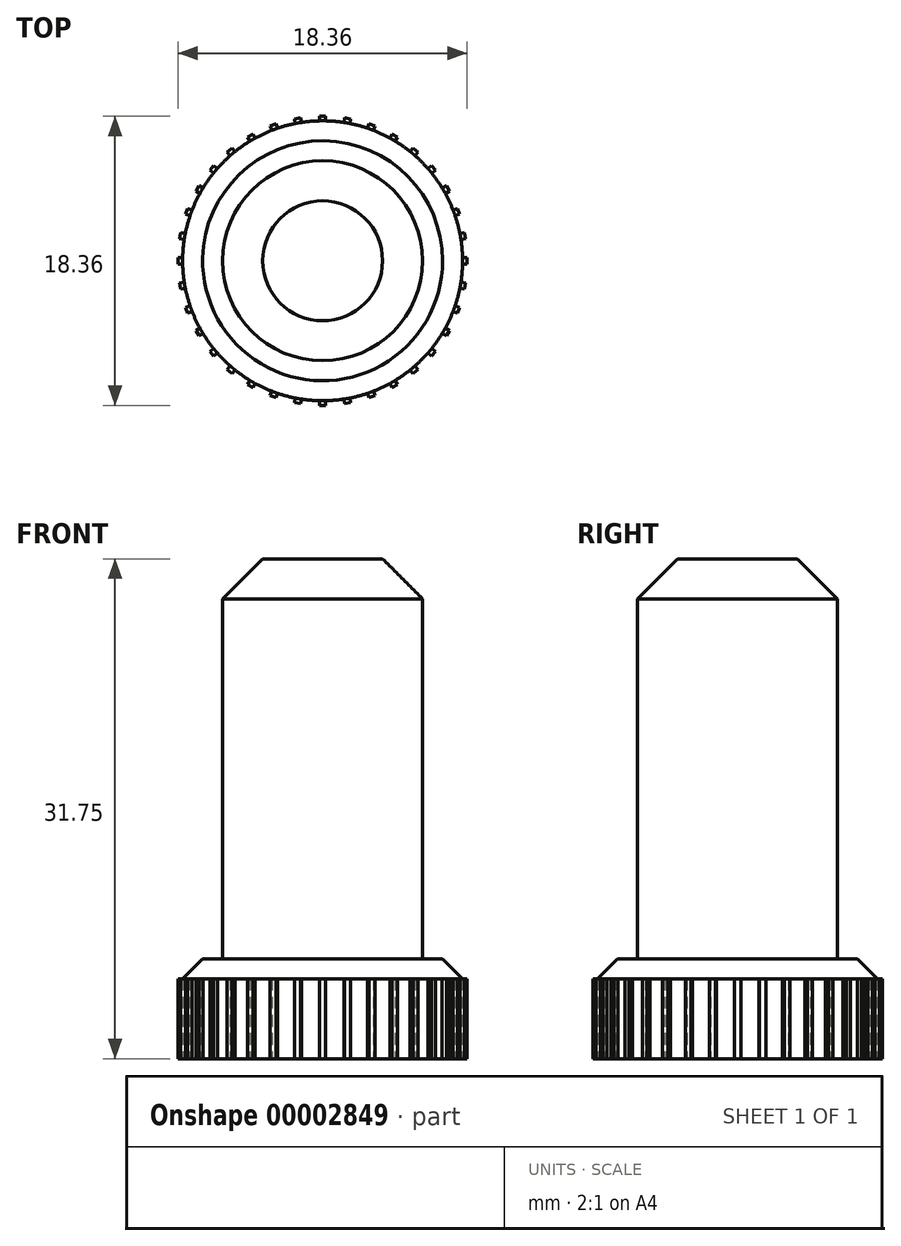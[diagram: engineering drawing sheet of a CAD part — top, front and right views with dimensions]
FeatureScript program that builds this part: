
annotation { "Feature Type Name" : "Feature", "Feature Type Description" : "" }
export const myFeature = defineFeature(function(context is Context, id is Id, definition is map)
    precondition{}
    {
        {
            var Q0;
            Q0=qCreatedBy(makeId("Top.planeOp"),FACE);
            var sketch = newSketch(context, id + "F0", { "sketchPlane" : qUnion([Q0])});
            skCircle(sketch, "E0", {"center": v(0, 0) * mm, "radius": 8.9 * mm});
            skSolve(sketch);
        }
        {
            var Q0;
            Q0=makeQuery(id+"F0.imprint","IMPRINT",FACE,{"disambiguationData":[TD([[makeQuery(id+"F0.imprint","IMPRINT",EDGE,{"derivedFrom":sQuery(id+"F0.wireOp",EDGE,"E0")}),1.0]])]});
            extrude(context, id + "F1", {"entities" : qUnion([Q0]), "depth" : 6.35 * mm});
        }
        {
            var Q0;
            Q0=makeQuery(id+"F1.opExtrude","CAP_FACE",FACE,{"disambiguationData":[OSD([sQuery(id+"F0.wireOp",EDGE,"E0")])],"isStart":false});
            var sketch = newSketch(context, id + "F2", { "sketchPlane" : qUnion([Q0])});
            skCircle(sketch, "E1", {"center": v(0, 0) * mm, "radius": 6.35 * mm});
            skSolve(sketch);
        }
        {
            var Q0;
            Q0=makeQuery(id+"F2.imprint","IMPRINT",FACE,{"disambiguationData":[TD([[makeQuery(id+"F2.imprint","IMPRINT",EDGE,{"derivedFrom":sQuery(id+"F2.wireOp",EDGE,"E1")}),1.0]])]});
            extrude(context, id + "F3", {"entities" : qUnion([Q0]), "operationType" : NewBodyOperationType.ADD, "depth" : 25.4 * mm});
        }
        {
            var Q0;
            Q0=makeQuery(id+"F3.opExtrude","CAP_EDGE",EDGE,{"disambiguationData":[OSD([sQuery(id+"F2.wireOp",EDGE,"E1")])],"isStart":false});
            chamfer(context, id + "F4", {"entities" : qUnion([Q0]), "width" : 2.54 * mm, "tangentPropagation" : true});
        }
        {
            var Q0;
            Q0=makeQuery(id+"F1.opExtrude","CAP_FACE",FACE,{"disambiguationData":[OSD([sQuery(id+"F0.wireOp",EDGE,"E0")])],"isStart":true});
            var sketch = newSketch(context, id + "F5", { "sketchPlane" : qUnion([Q0])});
            skLineSegment(sketch, "E2", {"start": v(0, 0) * mm, "end": v(-8.9, 0) * mm, "construction": true});
            skLineSegment(sketch, "E3.rect.bottom", {"start": v(-9.18, 0.2) * mm, "end": v(-8.89, 0.2) * mm});
            skLineSegment(sketch, "E3.rect.top", {"start": v(-9.18, -0.2) * mm, "end": v(-8.89, -0.2) * mm});
            skLineSegment(sketch, "E3.rect.left", {"start": v(-9.18, 0.2) * mm, "end": v(-9.18, -0.2) * mm});
            skPoint(sketch, "E3.rect.middle", {"position": v(-8.9, 0) * mm});
            skCircle(sketch, "E4", {"center": v(0, 0) * mm, "radius": 8.9 * mm, "construction": true});
            skSolve(sketch);
        }
        {
            var Q0;
            {var subQ2=sQuery(id+"F5.wireOp",EDGE,"E3.rect.bottom");Q0=makeQuery(id+"F5.imprint","IMPRINT",FACE,{"disambiguationData":[TD([[makeQuery(id+"F5.imprint","IMPRINT",EDGE,{"derivedFrom":subQ2}),-1.0]])]});}
            var Q1;
            Q1=makeQuery(id+"F3.opExtrude","SWEPT_FACE",FACE,{"disambiguationData":[OSD([sQuery(id+"F2.wireOp",EDGE,"E1")])]});
            extrude(context, id + "F6", {"entities" : qUnion([Q0]), "operationType" : NewBodyOperationType.ADD, "oppositeDirection" : true, "endBoundEntity" : qUnion([Q1]), "depth" : 5.08 * mm});
        }
        {
            var Q0;
            Q0=makeQuery(id+"F6.opExtrude","SWEPT_FACE",FACE,{"disambiguationData":[OSD([sQuery(id+"F5.wireOp",EDGE,"E3.rect.bottom")])]});
            var Q1;
            Q1=makeQuery(id+"F6.opExtrude","SWEPT_FACE",FACE,{"disambiguationData":[OSD([sQuery(id+"F5.wireOp",EDGE,"E3.rect.left")])]});
            var Q2;
            Q2=makeQuery(id+"F6.opExtrude","SWEPT_FACE",FACE,{"disambiguationData":[OSD([sQuery(id+"F5.wireOp",EDGE,"E3.rect.top")])]});
            var Q3;
            Q3=makeQuery(id+"F6.opExtrude","CAP_FACE",FACE,{"disambiguationData":[OSD([sQuery(id+"F0.wireOp",EDGE,"E0"),sQuery(id+"F5.wireOp",EDGE,"E3.rect.bottom"),sQuery(id+"F5.wireOp",EDGE,"E3.rect.top"),sQuery(id+"F5.wireOp",EDGE,"E3.rect.left")])],"isStart":false});
            var Q4;
            Q4=makeQuery(id+"F1.opExtrude","CAP_EDGE",EDGE,{"disambiguationData":[OSD([sQuery(id+"F0.wireOp",EDGE,"E0")])],"isStart":true});
            circularPattern(context, id + "F7", {"faces" : qUnion([Q0, Q1, Q2, Q3]), "axis" : qUnion([Q4]), "angle" : 360 * degree, "instanceCount" : 36, "equalSpace" : true, "patternType" : PatternType.FACE});
        }
        {
            var Q0;
            Q0=makeQuery(id+"F1.opExtrude","CAP_EDGE",EDGE,{"disambiguationData":[OSD([sQuery(id+"F0.wireOp",EDGE,"E0")])],"isStart":false});
            chamfer(context, id + "F8", {"entities" : qUnion([Q0]), "width" : 1.27 * mm, "tangentPropagation" : true});
        }
    });
